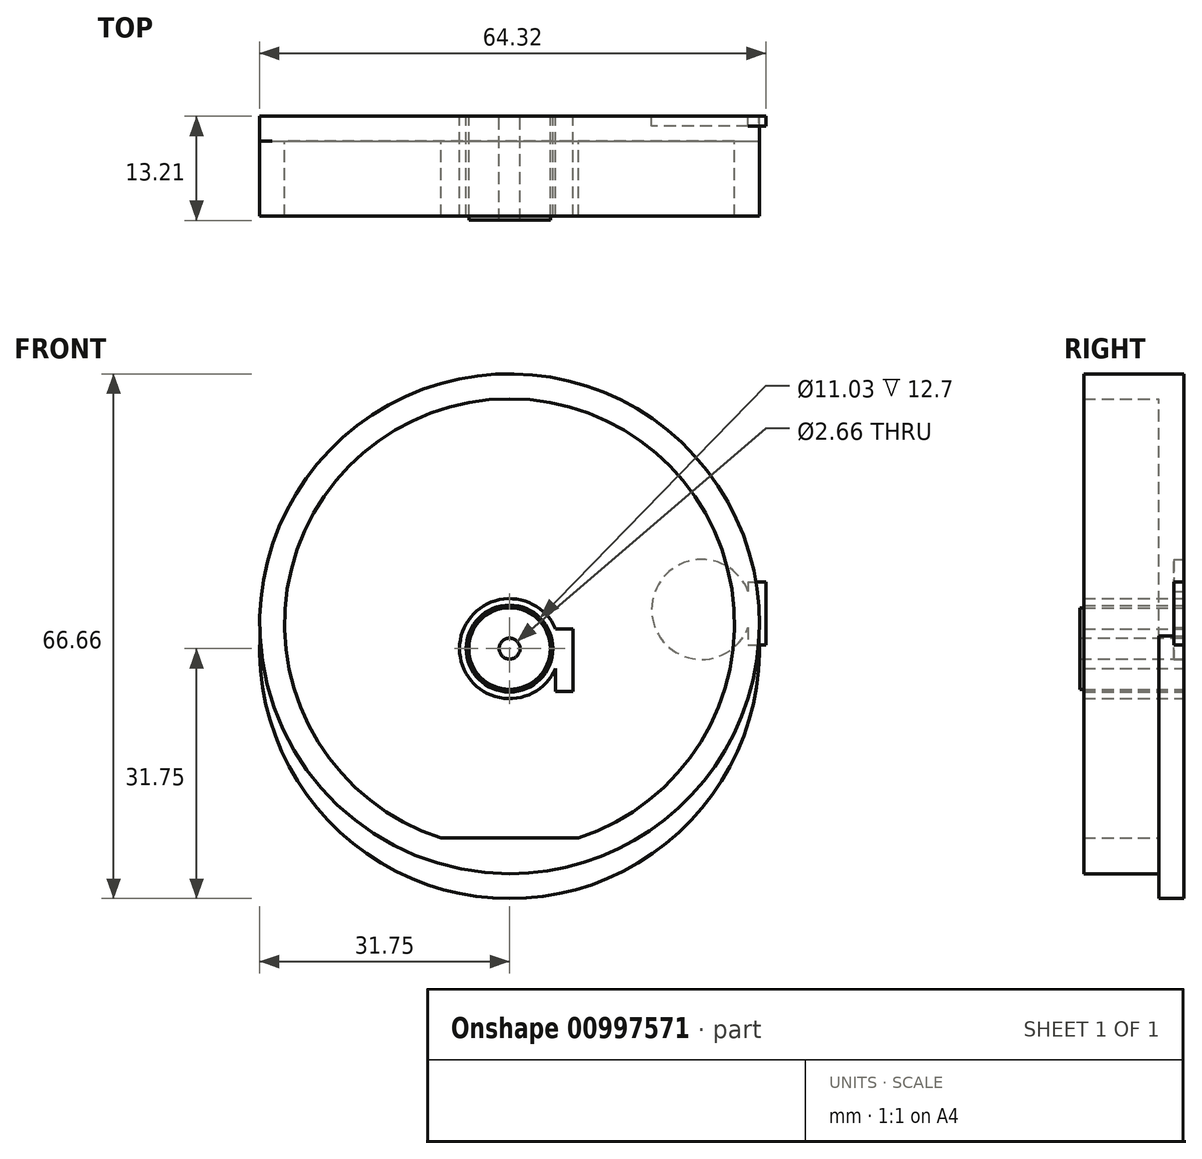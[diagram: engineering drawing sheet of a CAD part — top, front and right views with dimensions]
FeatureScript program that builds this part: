
annotation { "Feature Type Name" : "Feature", "Feature Type Description" : "" }
export const myFeature = defineFeature(function(context is Context, id is Id, definition is map)
    precondition{}
    {
        {
            var Q0;
            Q0=qCreatedBy(makeId("Front.planeOp"),FACE);
            var sketch = newSketch(context, id + "F0", { "sketchPlane" : qUnion([Q0])});
            skCircle(sketch, "E0", {"center": v(0, 3.16) * mm, "radius": 31.75 * mm});
            skCircle(sketch, "E1", {"center": v(0, 3.16) * mm, "radius": 28.58 * mm});
            skSolve(sketch);
        }
        {
            var Q0;
            Q0=makeQuery(id+"F0.imprint","IMPRINT",FACE,{"disambiguationData":[TD([[makeQuery(id+"F0.imprint","IMPRINT",EDGE,{"derivedFrom":sQuery(id+"F0.wireOp",EDGE,"E0")}),1.0]])]});
            extrude(context, id + "F1", {"entities" : qUnion([Q0]), "depth" : 12.7 * mm, "offsetDistance" : 25.4 * mm});
        }
        {
            var Q0;
            Q0=qCreatedBy(makeId("Front.planeOp"),FACE);
            var sketch = newSketch(context, id + "F2", { "sketchPlane" : qUnion([Q0])});
            skCircle(sketch, "E2", {"center": v(0, 0) * mm, "radius": 31.75 * mm});
            skSolve(sketch);
        }
        {
            var Q0;
            Q0=makeQuery(id+"F2.imprint","IMPRINT",FACE,{"disambiguationData":[TD([[makeQuery(id+"F2.imprint","IMPRINT",EDGE,{"derivedFrom":sQuery(id+"F2.wireOp",EDGE,"E2")}),1.0]])]});
            extrude(context, id + "F3", {"entities" : qUnion([Q0]), "depth" : 3.17 * mm, "offsetDistance" : 25.4 * mm});
        }
        {
            var Q0;
            Q0=qCreatedBy(makeId("Front.planeOp"),FACE);
            var sketch = newSketch(context, id + "F4", { "sketchPlane" : qUnion([Q0])});
            skCircle(sketch, "E3", {"center": v(0, 0) * mm, "radius": 31.75 * mm});
            skSolve(sketch);
        }
        {
            var Q0;
            Q0=makeQuery(id+"F4.imprint","IMPRINT",FACE,{"disambiguationData":[TD([[makeQuery(id+"F4.imprint","IMPRINT",EDGE,{"derivedFrom":sQuery(id+"F4.wireOp",EDGE,"E3")}),1.0]])]});
            extrude(context, id + "F5", {"entities" : qUnion([Q0]), "depth" : 3.17 * mm, "offsetDistance" : 25.4 * mm});
        }
        {
            var Q0;
            Q0=qCreatedBy(makeId("Front.planeOp"),FACE);
            var sketch = newSketch(context, id + "F6", { "sketchPlane" : qUnion([Q0])});
            skLineSegment(sketch, "E4.bottom", {"start": v(10.72, -25.78) * mm, "end": v(-10.72, -25.78) * mm});
            skLineSegment(sketch, "E4.top", {"start": v(10.72, -24.05) * mm, "end": v(-10.72, -24.05) * mm});
            skLineSegment(sketch, "E4.left", {"start": v(10.72, -25.78) * mm, "end": v(10.72, -24.05) * mm});
            skLineSegment(sketch, "E4.right", {"start": v(-10.72, -25.78) * mm, "end": v(-10.72, -24.05) * mm});
            skPoint(sketch, "E4.middle", {"position": v(0, -24.92) * mm});
            skSolve(sketch);
        }
        {
            var Q0;
            Q0 = qSketchRegion(id + "F6", true);
            extrude(context, id + "F7", {"entities" : qUnion([Q0]), "operationType" : NewBodyOperationType.ADD, "depth" : 12.7 * mm, "offsetDistance" : 25.4 * mm});
        }
        {
            var Q0;
            Q0=qCreatedBy(makeId("Front.planeOp"),FACE);
            var sketch = newSketch(context, id + "F8", { "sketchPlane" : qUnion([Q0])});
            skCircle(sketch, "E5", {"center": v(0, 0) * mm, "radius": 6.35 * mm});
            skCircle(sketch, "E6", {"center": v(0, 0) * mm, "radius": 5.51 * mm});
            skCircle(sketch, "E7", {"center": v(0, 0) * mm, "radius": 5.17 * mm});
            skCircle(sketch, "E8", {"center": v(0, 0) * mm, "radius": 1.33 * mm});
            skCircle(sketch, "E9", {"center": v(24.4, 4.98) * mm, "radius": 6.35 * mm});
            skLineSegment(sketch, "E10.bottom", {"start": v(5.83, 2.5) * mm, "end": v(8.09, 2.5) * mm});
            skLineSegment(sketch, "E10.top", {"start": v(5.83, -5.46) * mm, "end": v(8.09, -5.46) * mm});
            skLineSegment(sketch, "E10.left", {"start": v(5.83, 2.5) * mm, "end": v(5.83, -5.46) * mm});
            skLineSegment(sketch, "E10.right", {"start": v(8.09, 2.5) * mm, "end": v(8.09, -5.46) * mm});
            skLineSegment(sketch, "E11.bottom", {"start": v(30.32, 8.45) * mm, "end": v(32.57, 8.45) * mm});
            skLineSegment(sketch, "E11.top", {"start": v(30.32, 0.48) * mm, "end": v(32.57, 0.48) * mm});
            skLineSegment(sketch, "E11.left", {"start": v(30.32, 8.45) * mm, "end": v(30.32, 0.48) * mm});
            skLineSegment(sketch, "E11.right", {"start": v(32.57, 8.45) * mm, "end": v(32.57, 0.48) * mm});
            skSolve(sketch);
        }
        {
            var Q0;
            Q0=makeQuery(id+"F8.imprint","IMPRINT",FACE,{"disambiguationData":[TD([[makeQuery(id+"F8.imprint","IMPRINT",EDGE,{"derivedFrom":sQuery(id+"F8.wireOp",EDGE,"E6")}),-1.0]])]});
            var Q1;
            {var subQ4=sQuery(id+"F8.wireOp",EDGE,"E10.bottom");Q1=makeQuery(id+"F8.imprint","IMPRINT",FACE,{"disambiguationData":[TD([[makeQuery(id+"F8.imprint","IMPRINT",EDGE,{"derivedFrom":subQ4}),-1.0]])]});}
            var Q2;
            {var subQ0=sQuery(id+"F8.wireOp",EDGE,"E10.left");var subQ1=sQuery(id+"F8.wireOp",EDGE,"E5");var subQ3=makeQuery(id+"F8.imprint","INTERSECT",VERTEX,{"derivedFrom":[subQ1,subQ0]});Q2=makeQuery(id+"F8.imprint","IMPRINT",FACE,{"disambiguationData":[TD([[makeQuery(id+"F8.imprint","IMPRINT",EDGE,{"disambiguationData":[TD([[subQ3,-1.0]])],"derivedFrom":subQ1}),1.0]])]});}
            extrude(context, id + "F9", {"entities" : qUnion([Q0, Q1, Q2]), "depth" : 12.7 * mm, "offsetDistance" : 25.4 * mm});
        }
        {
            var Q0;
            Q0=makeQuery(id+"F8.imprint","IMPRINT",FACE,{"disambiguationData":[TD([[makeQuery(id+"F8.imprint","IMPRINT",EDGE,{"derivedFrom":sQuery(id+"F8.wireOp",EDGE,"E9")}),1.0]])]});
            var Q1;
            {var subQ1=sQuery(id+"F8.wireOp",EDGE,"E11.bottom");Q1=makeQuery(id+"F8.imprint","IMPRINT",FACE,{"disambiguationData":[TD([[makeQuery(id+"F8.imprint","IMPRINT",EDGE,{"derivedFrom":subQ1}),-1.0]])]});}
            extrude(context, id + "F10", {"entities" : qUnion([Q0, Q1]), "depth" : 1.27 * mm, "offsetDistance" : 25.4 * mm});
        }
        {
            var Q0;
            Q0=makeQuery(id+"F8.imprint","IMPRINT",FACE,{"disambiguationData":[TD([[makeQuery(id+"F8.imprint","IMPRINT",EDGE,{"derivedFrom":sQuery(id+"F8.wireOp",EDGE,"E7")}),1.0]])]});
            extrude(context, id + "F11", {"entities" : qUnion([Q0]), "depth" : 13.2 * mm, "offsetDistance" : 25.4 * mm});
        }
    });
